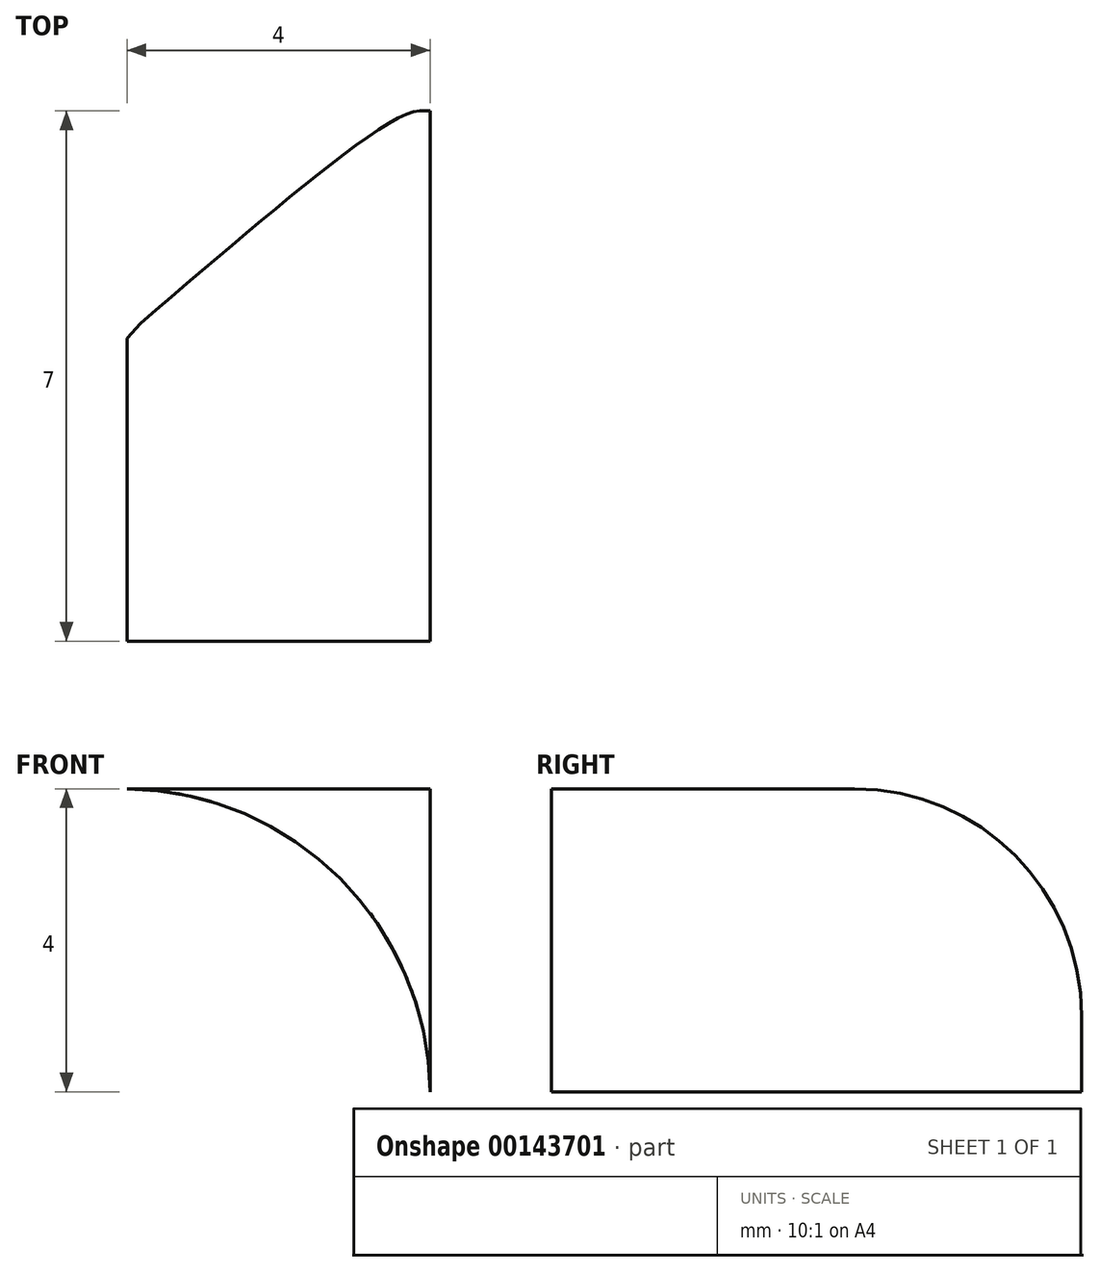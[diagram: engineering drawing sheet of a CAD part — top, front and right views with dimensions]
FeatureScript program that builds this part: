
annotation { "Feature Type Name" : "Feature", "Feature Type Description" : "" }
export const myFeature = defineFeature(function(context is Context, id is Id, definition is map)
    precondition{}
    {
        {
            var Q0;
            Q0=qCreatedBy(makeId("Top.planeOp"),FACE);
            var sketch = newSketch(context, id + "F0", { "sketchPlane" : qUnion([Q0]), "disableImprinting" : false});
            skLineSegment(sketch, "E0", {"start": v(0, 0) * mm, "end": v(0, -43.48) * mm, "construction": true});
            skLineSegment(sketch, "E1", {"start": v(0, 0) * mm, "end": v(-5.75, 0) * mm, "construction": true});
            skLineSegment(sketch, "E2", {"start": v(-5.75, 0) * mm, "end": v(-5.75, -17) * mm});
            skLineSegment(sketch, "E3", {"start": v(-5.75, -17) * mm, "end": v(-20, -17) * mm});
            skLineSegment(sketch, "E4", {"start": v(-20, -17) * mm, "end": v(-20, -24) * mm});
            skLineSegment(sketch, "E5", {"start": v(-20, -24) * mm, "end": v(0, -24) * mm});
            skPoint(sketch, "E6", {"position": v(0, -2.5) * mm});
            skLineSegment(sketch, "E7.MirrorCS", {"start": v(20, -24) * mm, "end": v(0, -24) * mm});
            skLineSegment(sketch, "E8.MirrorCS", {"start": v(20, -17) * mm, "end": v(20, -24) * mm});
            skLineSegment(sketch, "E9.MirrorCS", {"start": v(5.75, -17) * mm, "end": v(20, -17) * mm});
            skLineSegment(sketch, "E10.MirrorCS", {"start": v(5.75, 0) * mm, "end": v(5.75, -17) * mm});
            skArc(sketch, "E11", {"start": v(-5.75, 0) * mm, "mid": v(0, -2.5) * mm, "end": v(5.75, 0) * mm});
            skSolve(sketch);
        }
        {
            var Q0;
            Q0=makeQuery(id+"F0.imprint","IMPRINT",FACE,{"disambiguationData":[TD([[makeQuery(id+"F0.imprint","IMPRINT",EDGE,{"derivedFrom":sQuery(id+"F0.wireOp",EDGE,"E2")}),1.0]])]});
            extrude(context, id + "F1", {"entities" : qUnion([Q0]), "depth" : 8 * mm, "offsetDistance" : 25 * mm});
        }
        {
            var Q0;
            Q0=makeQuery(id+"F1.opExtrude","SWEPT_FACE",FACE,{"disambiguationData":[OSD([sQuery(id+"F0.wireOp",EDGE,"E2")])]});
            var sketch = newSketch(context, id + "F2", { "sketchPlane" : qUnion([Q0])});
            skLineSegment(sketch, "E12", {"start": v(0, 4) * mm, "end": v(11.41, 4) * mm, "construction": true});
            skPoint(sketch, "E13", {"position": v(4.5, 4) * mm});
            skArc(sketch, "E14", {"start": v(1.64, 8) * mm, "mid": v(0.67, 7.38) * mm, "end": v(0, 6.44) * mm});
            skArc(sketch, "E15.MirrorCS", {"start": v(1.64, 0) * mm, "mid": v(0.67, 0.62) * mm, "end": v(0, 1.56) * mm});
            skSolve(sketch);
        }
        {
            var Q0;
            Q0=sQuery(id+"F2.wireOp",VERTEX,"E13");
            var Q1;
            Q1=makeQuery(id+"F1.opExtrude","SWEPT_BODY",BODY,{"disambiguationData":[OSD([sQuery(id+"F0.wireOp",EDGE,"E2"),sQuery(id+"F0.wireOp",EDGE,"E3"),sQuery(id+"F0.wireOp",EDGE,"E4"),sQuery(id+"F0.wireOp",EDGE,"E5"),sQuery(id+"F0.wireOp",EDGE,"E7.MirrorCS"),sQuery(id+"F0.wireOp",EDGE,"E8.MirrorCS"),sQuery(id+"F0.wireOp",EDGE,"E9.MirrorCS"),sQuery(id+"F0.wireOp",EDGE,"E10.MirrorCS"),sQuery(id+"F0.wireOp",EDGE,"E11")])]});
            hole(context, id + "F3", {"style" : HoleStyle.SIMPLE, "endStyle" : HoleEndStyle.THROUGH, "holeDiameter" : 3.2 * mm, "majorDiameter" : 5 * mm, "isTappedThrough" : true, "tappedDepth" : 12 * mm, "tapClearance" : 3, "locations" : qUnion([Q0]), "scope" : qUnion([Q1]), "startStyle" : HoleStartStyle.PART});
        }
        {
            var Q0;
            Q0=makeQuery(id+"F1.opExtrude","SWEPT_EDGE",EDGE,{"disambiguationData":[OSD([sQuery(id+"F0.wireOp",EDGE,"E2"),sQuery(id+"F0.wireOp",EDGE,"E11")])]});
            var Q1;
            Q1=makeQuery(id+"F1.opExtrude","SWEPT_EDGE",EDGE,{"disambiguationData":[OSD([sQuery(id+"F0.wireOp",EDGE,"E10.MirrorCS"),sQuery(id+"F0.wireOp",EDGE,"E11")])]});
            fillet(context, id + "F4", {"entities" : qUnion([Q0, Q1]), "tangentPropagation" : true, "crossSection" : FilletCrossSection.CURVATURE, "radius" : 2 * mm, "magnitude" : 0.5, "defaultsChanged" : true, "vertexSettings" : []});
        }
        {
            var Q0;
            Q0=makeQuery(id+"F1.opExtrude","CAP_EDGE",EDGE,{"disambiguationData":[OSD([sQuery(id+"F0.wireOp",EDGE,"E9.MirrorCS")])],"isStart":false});
            var Q1;
            Q1=makeQuery(id+"F1.opExtrude","CAP_EDGE",EDGE,{"disambiguationData":[OSD([sQuery(id+"F0.wireOp",EDGE,"E3")])],"isStart":false});
            fillet(context, id + "F5", {"entities" : qUnion([Q0, Q1]), "tangentPropagation" : true, "radius" : 3 * mm, "defaultsChanged" : true, "vertexSettings" : [], "allowEdgeOverflow" : false});
        }
        {
            var Q0;
            Q0=makeQuery(id+"F1.opExtrude","CAP_EDGE",EDGE,{"disambiguationData":[OSD([sQuery(id+"F0.wireOp",EDGE,"E9.MirrorCS")])],"isStart":true});
            var Q1;
            Q1=makeQuery(id+"F1.opExtrude","CAP_EDGE",EDGE,{"disambiguationData":[OSD([sQuery(id+"F0.wireOp",EDGE,"E3")])],"isStart":true});
            fillet(context, id + "F6", {"entities" : qUnion([Q0, Q1]), "tangentPropagation" : true, "radius" : 3 * mm, "defaultsChanged" : true, "vertexSettings" : [], "allowEdgeOverflow" : false});
        }
        {
            var Q0;
            Q0=makeQuery(id+"F1.opExtrude","SWEPT_FACE",FACE,{"disambiguationData":[OSD([sQuery(id+"F0.wireOp",EDGE,"E5"),sQuery(id+"F0.wireOp",EDGE,"E7.MirrorCS")])]});
            var sketch = newSketch(context, id + "F7", { "sketchPlane" : qUnion([Q0])});
            skLineSegment(sketch, "E16", {"start": v(0, 0) * mm, "end": v(0, 8) * mm, "construction": true});
            skLineSegment(sketch, "E17", {"start": v(0, 4) * mm, "end": v(-20, 4) * mm, "construction": true});
            skPoint(sketch, "E18", {"position": v(-16, 4) * mm});
            skPoint(sketch, "E19.MirrorP", {"position": v(16, 4) * mm});
            skArc(sketch, "E20", {"start": v(-16, 8) * mm, "mid": v(-18.81, 6.81) * mm, "end": v(-20, 4) * mm});
            skArc(sketch, "E21.MirrorCS", {"start": v(16, 8) * mm, "mid": v(18.81, 6.81) * mm, "end": v(20, 4) * mm});
            skSolve(sketch);
        }
        {
            var Q0;
            Q0=sQuery(id+"F7.wireOp",VERTEX,"E18");
            var Q1;
            Q1=sQuery(id+"F7.wireOp",VERTEX,"E19.MirrorP");
            var Q2;
            Q2=makeQuery(id+"F1.opExtrude","SWEPT_BODY",BODY,{"disambiguationData":[OSD([sQuery(id+"F0.wireOp",EDGE,"E2"),sQuery(id+"F0.wireOp",EDGE,"E3"),sQuery(id+"F0.wireOp",EDGE,"E4"),sQuery(id+"F0.wireOp",EDGE,"E5"),sQuery(id+"F0.wireOp",EDGE,"E7.MirrorCS"),sQuery(id+"F0.wireOp",EDGE,"E8.MirrorCS"),sQuery(id+"F0.wireOp",EDGE,"E9.MirrorCS"),sQuery(id+"F0.wireOp",EDGE,"E10.MirrorCS"),sQuery(id+"F0.wireOp",EDGE,"E11")])]});
            hole(context, id + "F8", {"style" : HoleStyle.SIMPLE, "endStyle" : HoleEndStyle.THROUGH, "standardTappedOrClearance" : lookupTablePath({ "fit" : "Close", "standard" : "ISO", "size" : "M3", "type" : "Clearance" }), "standardBlindInLast" : lookupTablePath({ "fit" : "Close", "standard" : "ISO", "engagement" : "75%", "pitch" : "0.5 mm", "size" : "M3", "type" : "Clearance & tapped" }), "holeDiameter" : 3.2 * mm, "majorDiameter" : 3 * mm, "isTappedThrough" : true, "tappedDepth" : 12 * mm, "tapClearance" : 3, "locations" : qUnion([Q0, Q1]), "scope" : qUnion([Q2]), "startStyle" : HoleStartStyle.PART});
        }
        {
            var Q0;
            {var subQ0=sQuery(id+"F7.wireOp",EDGE,"E20");Q0=makeQuery(id+"F7.imprint","IMPRINT",FACE,{"disambiguationData":[TD([[makeQuery(id+"F7.imprint","IMPRINT",EDGE,{"derivedFrom":subQ0}),-1.0]])]});}
            var Q1;
            {var subQ0=sQuery(id+"F7.wireOp",EDGE,"E21.MirrorCS");Q1=makeQuery(id+"F7.imprint","IMPRINT",FACE,{"disambiguationData":[TD([[makeQuery(id+"F7.imprint","IMPRINT",EDGE,{"derivedFrom":subQ0}),1.0]])]});}
            extrude(context, id + "F9", {"entities" : qUnion([Q0, Q1]), "operationType" : NewBodyOperationType.REMOVE, "oppositeDirection" : true, "depth" : 25 * mm, "offsetDistance" : 25 * mm});
        }
    });
